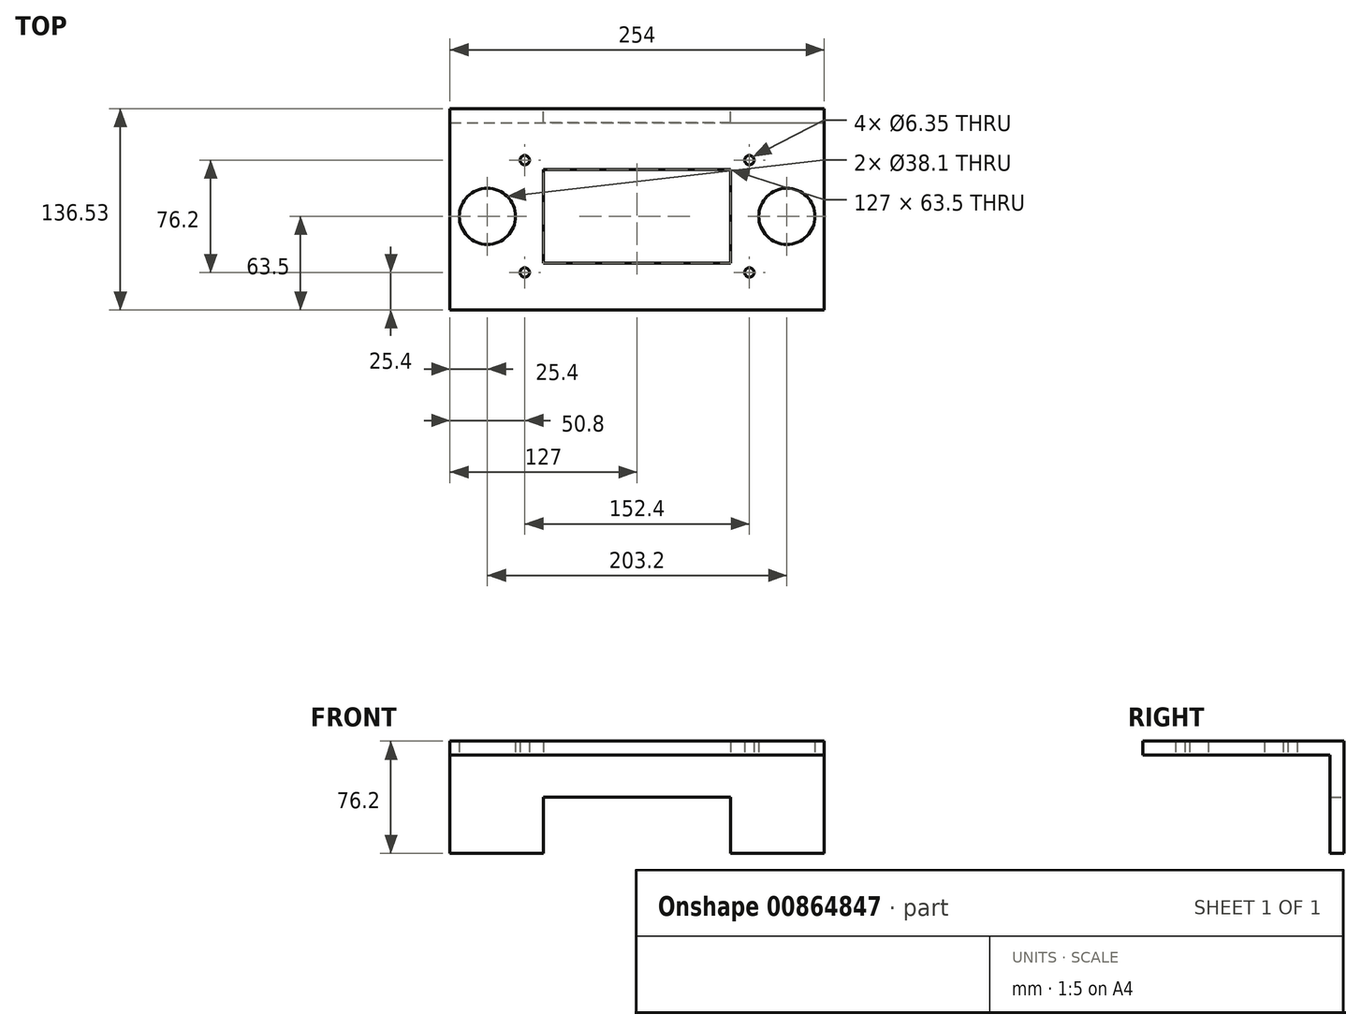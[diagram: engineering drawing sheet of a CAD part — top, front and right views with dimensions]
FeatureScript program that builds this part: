
annotation { "Feature Type Name" : "Feature", "Feature Type Description" : "" }
export const myFeature = defineFeature(function(context is Context, id is Id, definition is map)
    precondition{}
    {
        {
            var Q0;
            Q0=qCreatedBy(makeId("Top.planeOp"),FACE);
            var sketch = newSketch(context, id + "F0", { "sketchPlane" : qUnion([Q0])});
            skLineSegment(sketch, "E0.bottom", {"start": v(-127, 63.5) * mm, "end": v(127, 63.5) * mm});
            skLineSegment(sketch, "E0.top", {"start": v(-127, -63.5) * mm, "end": v(127, -63.5) * mm});
            skLineSegment(sketch, "E0.left", {"start": v(-127, 63.5) * mm, "end": v(-127, -63.5) * mm});
            skLineSegment(sketch, "E0.right", {"start": v(127, 63.5) * mm, "end": v(127, -63.5) * mm});
            skLineSegment(sketch, "E1", {"start": v(0, 63.5) * mm, "end": v(0, -63.5) * mm, "construction": true});
            skLineSegment(sketch, "E2", {"start": v(-127, 0) * mm, "end": v(127, 0) * mm, "construction": true});
            skLineSegment(sketch, "E3.bottom", {"start": v(-63.5, 31.75) * mm, "end": v(63.5, 31.75) * mm});
            skLineSegment(sketch, "E3.top", {"start": v(-63.5, -31.75) * mm, "end": v(63.5, -31.75) * mm});
            skLineSegment(sketch, "E3.left", {"start": v(-63.5, 31.75) * mm, "end": v(-63.5, -31.75) * mm});
            skLineSegment(sketch, "E3.right", {"start": v(63.5, 31.75) * mm, "end": v(63.5, -31.75) * mm});
            skLineSegment(sketch, "E4", {"start": v(0, 31.75) * mm, "end": v(0, -31.75) * mm, "construction": true});
            skLineSegment(sketch, "E5", {"start": v(-63.5, 0) * mm, "end": v(63.5, 0) * mm, "construction": true});
            skSolve(sketch);
        }
        {
            var Q0;
            Q0=makeQuery(id+"F0.imprint","IMPRINT",FACE,{"disambiguationData":[TD([[makeQuery(id+"F0.imprint","IMPRINT",EDGE,{"derivedFrom":sQuery(id+"F0.wireOp",EDGE,"E0.bottom")}),-1.0]])]});
            extrude(context, id + "F1", {"entities" : qUnion([Q0]), "depth" : 9.52 * mm, "offsetDistance" : 25.4 * mm});
        }
        {
            var Q0;
            Q0=qCreatedBy(makeId("Top.planeOp"),FACE);
            var sketch = newSketch(context, id + "F2", { "sketchPlane" : qUnion([Q0])});
            skCircle(sketch, "E6", {"center": v(-76.2, 38.1) * mm, "radius": 3.18 * mm});
            skCircle(sketch, "E7", {"center": v(76.2, 38.1) * mm, "radius": 3.18 * mm});
            skCircle(sketch, "E8", {"center": v(-76.2, -38.1) * mm, "radius": 3.18 * mm});
            skCircle(sketch, "E9", {"center": v(76.2, -38.1) * mm, "radius": 3.18 * mm});
            skSolve(sketch);
        }
        {
            var Q0;
            Q0 = qSketchRegion(id + "F2", true);
            extrude(context, id + "F3", {"entities" : qUnion([Q0]), "operationType" : NewBodyOperationType.REMOVE, "depth" : 9525 * mm, "offsetDistance" : 25.4 * mm});
        }
        {
            var Q0;
            Q0=qCreatedBy(makeId("Top.planeOp"),FACE);
            var sketch = newSketch(context, id + "F4", { "sketchPlane" : qUnion([Q0])});
            skCircle(sketch, "E10", {"center": v(-101.6, 0) * mm, "radius": 19.05 * mm});
            skCircle(sketch, "E11", {"center": v(101.6, 0) * mm, "radius": 19.05 * mm});
            skSolve(sketch);
        }
        {
            var Q0;
            Q0 = qSketchRegion(id + "F4", true);
            extrude(context, id + "F5", {"entities" : qUnion([Q0]), "operationType" : NewBodyOperationType.REMOVE, "endBound" : BoundingType.THROUGH_ALL, "depth" : 9.52 * mm, "offsetDistance" : 25.4 * mm});
        }
        {
            var Q0;
            Q0=makeQuery(id+"F1.opExtrude","SWEPT_FACE",FACE,{"disambiguationData":[OSD([sQuery(id+"F0.wireOp",EDGE,"E0.bottom")])]});
            var sketch = newSketch(context, id + "F6", { "sketchPlane" : qUnion([Q0])});
            skLineSegment(sketch, "E12.bottom", {"start": v(127, 9.53) * mm, "end": v(-127, 9.53) * mm});
            skLineSegment(sketch, "E12.top", {"start": v(127, -66.67) * mm, "end": v(-127, -66.68) * mm});
            skLineSegment(sketch, "E12.left", {"start": v(127, 9.53) * mm, "end": v(127, -66.67) * mm});
            skLineSegment(sketch, "E12.right", {"start": v(-127, 9.53) * mm, "end": v(-127, -66.68) * mm});
            skLineSegment(sketch, "E13", {"start": v(0, -66.67) * mm, "end": v(0, 9.52) * mm, "construction": true});
            skLineSegment(sketch, "E14", {"start": v(-127, -28.58) * mm, "end": v(127, -28.57) * mm, "construction": true});
            skSolve(sketch);
        }
        {
            var Q0;
            Q0 = qSketchRegion(id + "F6", true);
            extrude(context, id + "F7", {"entities" : qUnion([Q0]), "operationType" : NewBodyOperationType.ADD, "depth" : 9.52 * mm, "offsetDistance" : 25.4 * mm});
        }
        {
            var Q0;
            Q0=makeQuery(id+"F7.opExtrude","CAP_FACE",FACE,{"disambiguationData":[OSD([sQuery(id+"F6.wireOp",EDGE,"E12.bottom"),sQuery(id+"F6.wireOp",EDGE,"E12.top"),sQuery(id+"F6.wireOp",EDGE,"E12.left"),sQuery(id+"F6.wireOp",EDGE,"E12.right")])],"isStart":false});
            var sketch = newSketch(context, id + "F8", { "sketchPlane" : qUnion([Q0])});
            skLineSegment(sketch, "E15.bottom", {"start": v(-63.5, -28.58) * mm, "end": v(63.5, -28.58) * mm});
            skLineSegment(sketch, "E15.top", {"start": v(-63.5, -66.67) * mm, "end": v(63.5, -66.67) * mm});
            skLineSegment(sketch, "E15.left", {"start": v(-63.5, -28.58) * mm, "end": v(-63.5, -66.68) * mm});
            skLineSegment(sketch, "E15.right", {"start": v(63.5, -28.58) * mm, "end": v(63.5, -66.67) * mm});
            skLineSegment(sketch, "E16", {"start": v(0, -28.58) * mm, "end": v(0, -66.68) * mm, "construction": true});
            skSolve(sketch);
        }
        {
            var Q0;
            Q0 = qSketchRegion(id + "F8", true);
            extrude(context, id + "F9", {"entities" : qUnion([Q0]), "operationType" : NewBodyOperationType.REMOVE, "endBound" : BoundingType.THROUGH_ALL, "oppositeDirection" : true, "depth" : 25.4 * mm, "offsetDistance" : 25.4 * mm});
        }
    });
